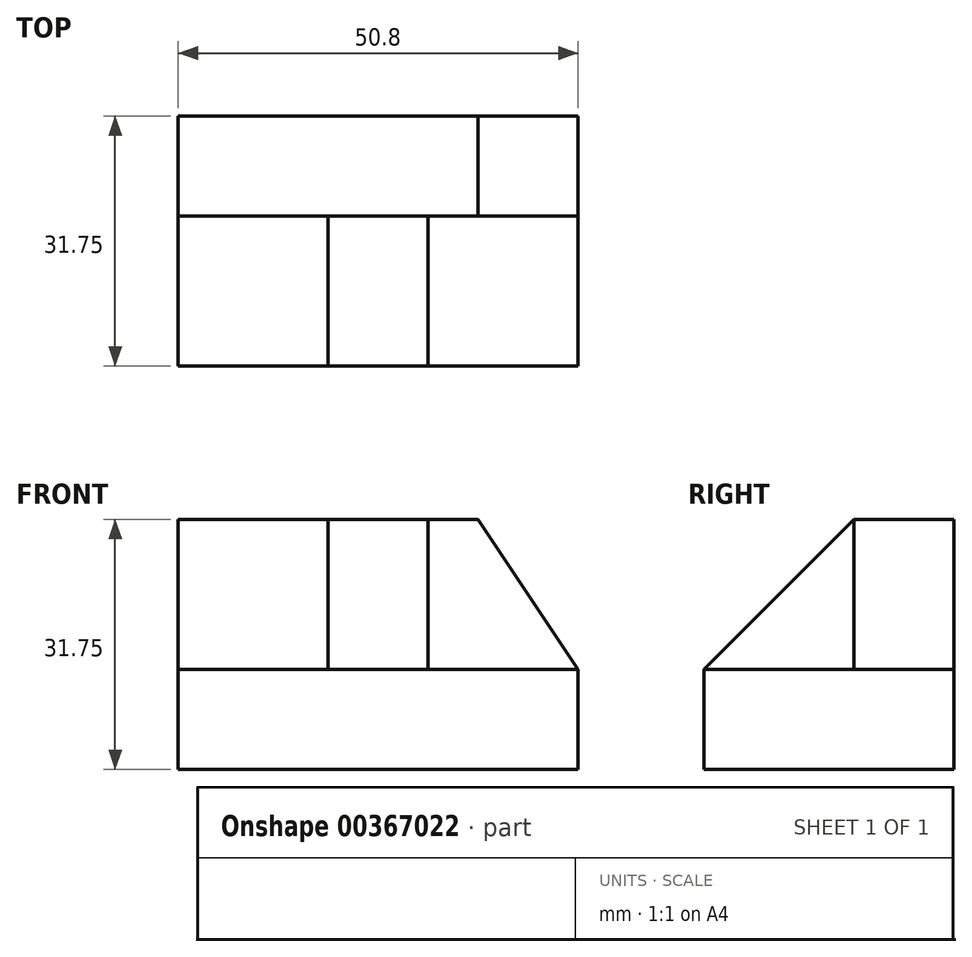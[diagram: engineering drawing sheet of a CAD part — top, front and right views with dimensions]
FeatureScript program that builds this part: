
annotation { "Feature Type Name" : "Feature", "Feature Type Description" : "" }
export const myFeature = defineFeature(function(context is Context, id is Id, definition is map)
    precondition{}
    {
        {
            var Q0;
            Q0=qCreatedBy(makeId("Front.planeOp"),FACE);
            var sketch = newSketch(context, id + "F0", { "sketchPlane" : qUnion([Q0])});
            skLineSegment(sketch, "E0", {"start": v(0, 0) * mm, "end": v(50.8, 0) * mm});
            skLineSegment(sketch, "E1", {"start": v(50.8, 0) * mm, "end": v(50.8, 31.75) * mm});
            skLineSegment(sketch, "E2", {"start": v(50.8, 31.75) * mm, "end": v(0, 31.75) * mm});
            skLineSegment(sketch, "E3", {"start": v(0, 31.75) * mm, "end": v(0, 0) * mm});
            skSolve(sketch);
        }
        {
            var Q0;
            Q0=makeQuery(id+"F0.imprint","IMPRINT",FACE,{"disambiguationData":[TD([[makeQuery(id+"F0.imprint","IMPRINT",EDGE,{"derivedFrom":sQuery(id+"F0.wireOp",EDGE,"E0")}),1.0]])]});
            extrude(context, id + "F1", {"entities" : qUnion([Q0]), "depth" : 31.75 * mm});
        }
        {
            var Q0;
            Q0=makeQuery(id+"F1.opExtrude","SWEPT_FACE",FACE,{"disambiguationData":[OSD([sQuery(id+"F0.wireOp",EDGE,"E2")])]});
            var sketch = newSketch(context, id + "F2", { "sketchPlane" : qUnion([Q0])});
            skLineSegment(sketch, "E4", {"start": v(31.75, -31.75) * mm, "end": v(31.75, -12.7) * mm});
            skLineSegment(sketch, "E5", {"start": v(31.75, -12.7) * mm, "end": v(50.8, -12.7) * mm});
            skLineSegment(sketch, "E6", {"start": v(50.8, -12.7) * mm, "end": v(50.8, -31.75) * mm});
            skLineSegment(sketch, "E7", {"start": v(50.8, -31.75) * mm, "end": v(31.75, -31.75) * mm});
            skSolve(sketch);
        }
        {
            var Q0;
            Q0=makeQuery(id+"F2.imprint","IMPRINT",FACE,{"disambiguationData":[TD([[makeQuery(id+"F2.imprint","IMPRINT",EDGE,{"derivedFrom":sQuery(id+"F2.wireOp",EDGE,"E4")}),-1.0]])]});
            extrude(context, id + "F3", {"entities" : qUnion([Q0]), "operationType" : NewBodyOperationType.REMOVE, "oppositeDirection" : true, "depth" : 19.05 * mm});
        }
        {
            var Q0;
            Q0=makeQuery(id+"F1.opExtrude","CAP_FACE",FACE,{"disambiguationData":[OSD([sQuery(id+"F0.wireOp",EDGE,"E0"),sQuery(id+"F0.wireOp",EDGE,"E1"),sQuery(id+"F0.wireOp",EDGE,"E2"),sQuery(id+"F0.wireOp",EDGE,"E3")])],"isStart":true});
            var sketch = newSketch(context, id + "F4", { "sketchPlane" : qUnion([Q0])});
            skLineSegment(sketch, "E8", {"start": v(-38.1, 31.75) * mm, "end": v(-50.8, 12.7) * mm});
            skSolve(sketch);
        }
        {
            var Q0;
            {var subQ0=sQuery(id+"F4.wireOp",EDGE,"E8");Q0=makeQuery(id+"F4.imprint","IMPRINT",FACE,{"disambiguationData":[TD([[makeQuery(id+"F4.imprint","IMPRINT",EDGE,{"derivedFrom":subQ0}),-1.0]])]});}
            extrude(context, id + "F5", {"entities" : qUnion([Q0]), "operationType" : NewBodyOperationType.REMOVE, "oppositeDirection" : true, "depth" : 12.7 * mm});
        }
        {
            var Q0;
            Q0=makeQuery(id+"F3.boolean.opBoolean","COPY",FACE,{"derivedFrom":makeQuery(id+"F3.opExtrude","SWEPT_FACE",FACE,{"disambiguationData":[OSD([sQuery(id+"F2.wireOp",EDGE,"E4")])]})});
            var sketch = newSketch(context, id + "F6", { "sketchPlane" : qUnion([Q0])});
            skLineSegment(sketch, "E9", {"start": v(-12.7, 31.75) * mm, "end": v(-31.75, 12.7) * mm});
            skSolve(sketch);
        }
        {
            var Q0;
            Q0=makeQuery(id+"F6.imprint","IMPRINT",FACE,{"disambiguationData":[TD([[makeQuery(id+"F6.imprint","IMPRINT",EDGE,{"derivedFrom":sQuery(id+"F6.wireOp",EDGE,"E9")}),-1.0]])]});
            extrude(context, id + "F7", {"entities" : qUnion([Q0]), "operationType" : NewBodyOperationType.REMOVE, "oppositeDirection" : true, "depth" : 12.7 * mm});
        }
        {
            var Q0;
            Q0=makeQuery(id+"F1.opExtrude","CAP_FACE",FACE,{"disambiguationData":[OSD([sQuery(id+"F0.wireOp",EDGE,"E0"),sQuery(id+"F0.wireOp",EDGE,"E1"),sQuery(id+"F0.wireOp",EDGE,"E2"),sQuery(id+"F0.wireOp",EDGE,"E3")])],"isStart":false});
            var sketch = newSketch(context, id + "F8", { "sketchPlane" : qUnion([Q0])});
            skLineSegment(sketch, "E10", {"start": v(19.05, 12.7) * mm, "end": v(0, 12.7) * mm});
            skSolve(sketch);
        }
        {
            var Q0;
            {var subQ0=sQuery(id+"F8.wireOp",EDGE,"E10");Q0=makeQuery(id+"F8.imprint","IMPRINT",FACE,{"disambiguationData":[TD([[makeQuery(id+"F8.imprint","IMPRINT",EDGE,{"derivedFrom":subQ0}),-1.0]])]});}
            extrude(context, id + "F9", {"entities" : qUnion([Q0]), "operationType" : NewBodyOperationType.REMOVE, "oppositeDirection" : true, "depth" : 19.05 * mm});
        }
    });
